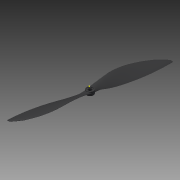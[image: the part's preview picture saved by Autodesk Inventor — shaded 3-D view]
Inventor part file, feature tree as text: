
AUTODESK INVENTOR PART (.ipt)
format: ipt  version: 2015 (Build 190159000, 159)  size: 299,520 bytes
history: native  units: in
note: dims shown in document units (in); Inventor stores cm internally (conversion verified against a paired STEP export)
features: other x2, sketch x1, imported_body x1
ambient origin geometry x8: Origin, YZ Plane, XZ Plane, XY Plane, X Axis, Y Axis, Z Axis, Center Point
bodies: Body1 (feature_tree)
feature tree (4):
  other  "Cut-Extrude3"
  other  "10x4.71"
  sketch  "Sketch1"
  imported_body  "Base1"
